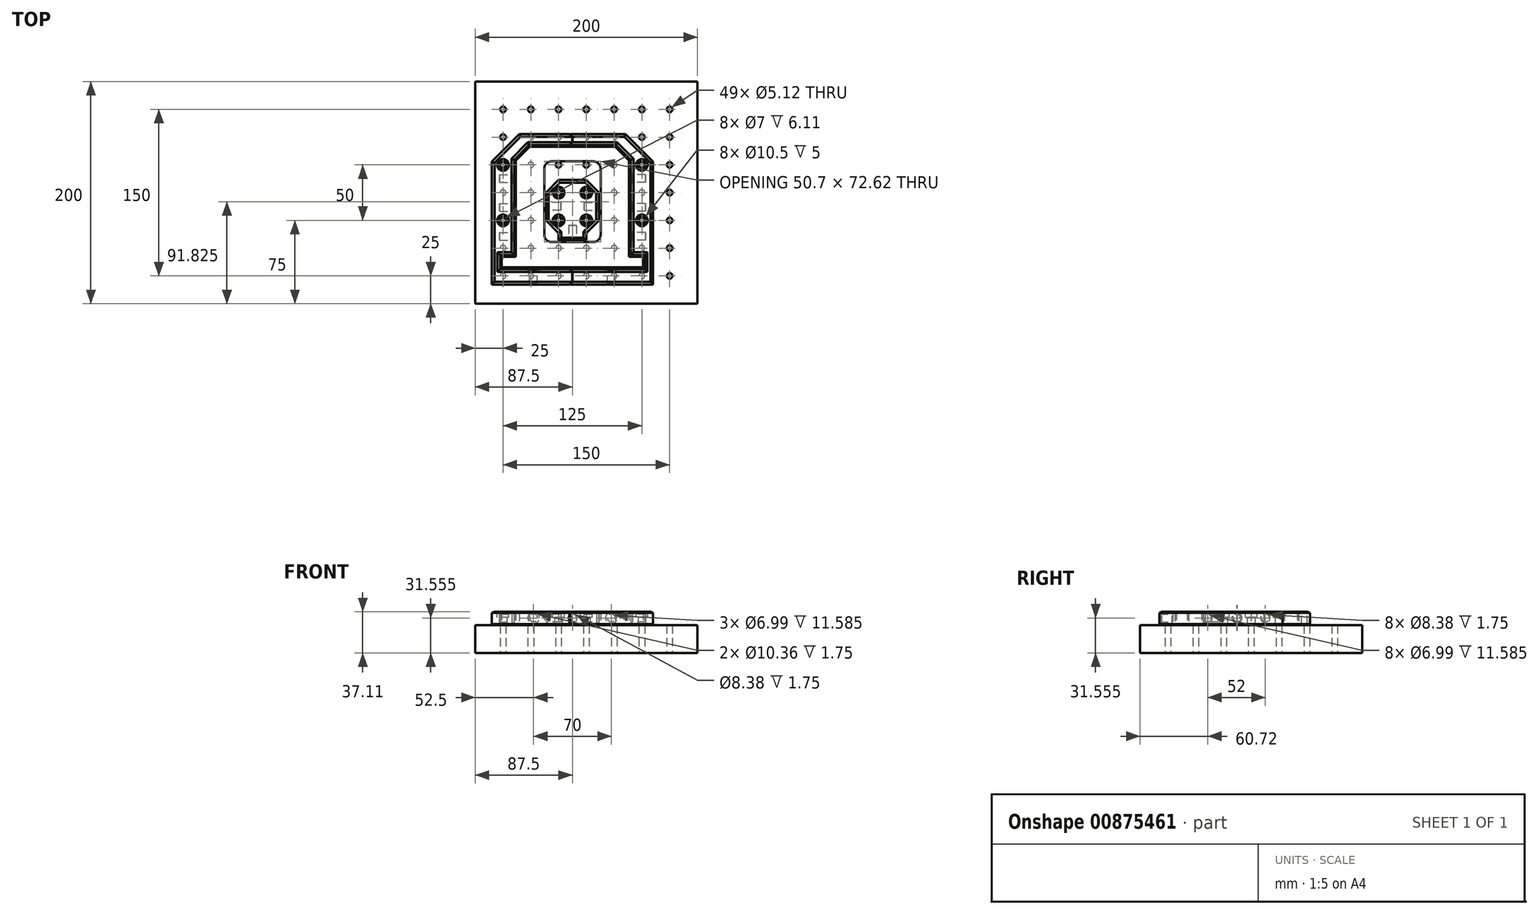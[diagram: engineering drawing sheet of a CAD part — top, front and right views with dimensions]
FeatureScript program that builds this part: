
annotation { "Feature Type Name" : "Feature", "Feature Type Description" : "" }
export const myFeature = defineFeature(function(context is Context, id is Id, definition is map)
    precondition{}
    {
        {
            assignVariable(context, id + "F0", {"name" : "plugdep1", "anyValue" : 13.33 * mm});
        }
        {
            assignVariable(context, id + "F1", {"name" : "plugdep2", "anyValue" : 1.75});
        }
        {
            var Q0;
            Q0=qCreatedBy(makeId("Top.planeOp"),FACE);
            var sketch = newSketch(context, id + "F2", { "sketchPlane" : qUnion([Q0])});
            skLineSegment(sketch, "E0.bottom", {"start": v(-100, 100) * mm, "end": v(100, 100) * mm});
            skLineSegment(sketch, "E0.top", {"start": v(-100, -100) * mm, "end": v(100, -100) * mm});
            skLineSegment(sketch, "E0.left", {"start": v(-100, 100) * mm, "end": v(-100, -100) * mm});
            skLineSegment(sketch, "E0.right", {"start": v(100, 100) * mm, "end": v(100, -100) * mm});
            skPoint(sketch, "E0.middle", {"position": v(0, 0) * mm});
            skCircle(sketch, "E1", {"center": v(-75, 75) * mm, "radius": 2.56 * mm});
            skCircle(sketch, "E2.0.1.0", {"center": v(-75, 50) * mm, "radius": 2.56 * mm});
            skCircle(sketch, "E2.0.2.0", {"center": v(-75, 25) * mm, "radius": 2.56 * mm});
            skCircle(sketch, "E2.0.3.0", {"center": v(-75, 0) * mm, "radius": 2.56 * mm});
            skCircle(sketch, "E2.0.4.0", {"center": v(-75, -25) * mm, "radius": 2.56 * mm});
            skCircle(sketch, "E2.0.5.0", {"center": v(-75, -50) * mm, "radius": 2.56 * mm});
            skCircle(sketch, "E2.0.6.0", {"center": v(-75, -75) * mm, "radius": 2.56 * mm});
            skCircle(sketch, "E2.1.0.0", {"center": v(-50, 75) * mm, "radius": 2.56 * mm});
            skCircle(sketch, "E2.1.1.0", {"center": v(-50, 50) * mm, "radius": 2.56 * mm});
            skCircle(sketch, "E2.1.2.0", {"center": v(-50, 25) * mm, "radius": 2.56 * mm});
            skCircle(sketch, "E2.1.3.0", {"center": v(-50, 0) * mm, "radius": 2.56 * mm});
            skCircle(sketch, "E2.1.4.0", {"center": v(-50, -25) * mm, "radius": 2.56 * mm});
            skCircle(sketch, "E2.1.5.0", {"center": v(-50, -50) * mm, "radius": 2.56 * mm});
            skCircle(sketch, "E2.1.6.0", {"center": v(-50, -75) * mm, "radius": 2.56 * mm});
            skCircle(sketch, "E2.2.0.0", {"center": v(-25, 75) * mm, "radius": 2.56 * mm});
            skCircle(sketch, "E2.2.1.0", {"center": v(-25, 50) * mm, "radius": 2.56 * mm});
            skCircle(sketch, "E2.2.2.0", {"center": v(-25, 25) * mm, "radius": 2.56 * mm});
            skCircle(sketch, "E2.2.3.0", {"center": v(-25, 0) * mm, "radius": 2.56 * mm});
            skCircle(sketch, "E2.2.4.0", {"center": v(-25, -25) * mm, "radius": 2.56 * mm});
            skCircle(sketch, "E2.2.5.0", {"center": v(-25, -50) * mm, "radius": 2.56 * mm});
            skCircle(sketch, "E2.2.6.0", {"center": v(-25, -75) * mm, "radius": 2.56 * mm});
            skCircle(sketch, "E2.3.0.0", {"center": v(0, 75) * mm, "radius": 2.56 * mm});
            skCircle(sketch, "E2.3.1.0", {"center": v(0, 50) * mm, "radius": 2.56 * mm});
            skCircle(sketch, "E2.3.2.0", {"center": v(0, 25) * mm, "radius": 2.56 * mm});
            skCircle(sketch, "E2.3.3.0", {"center": v(0, 0) * mm, "radius": 2.56 * mm});
            skCircle(sketch, "E2.3.4.0", {"center": v(0, -25) * mm, "radius": 2.56 * mm});
            skCircle(sketch, "E2.3.5.0", {"center": v(0, -50) * mm, "radius": 2.56 * mm});
            skCircle(sketch, "E2.3.6.0", {"center": v(0, -75) * mm, "radius": 2.56 * mm});
            skCircle(sketch, "E2.4.0.0", {"center": v(25, 75) * mm, "radius": 2.56 * mm});
            skCircle(sketch, "E2.4.1.0", {"center": v(25, 50) * mm, "radius": 2.56 * mm});
            skCircle(sketch, "E2.4.2.0", {"center": v(25, 25) * mm, "radius": 2.56 * mm});
            skCircle(sketch, "E2.4.3.0", {"center": v(25, 0) * mm, "radius": 2.56 * mm});
            skCircle(sketch, "E2.4.4.0", {"center": v(25, -25) * mm, "radius": 2.56 * mm});
            skCircle(sketch, "E2.4.5.0", {"center": v(25, -50) * mm, "radius": 2.56 * mm});
            skCircle(sketch, "E2.4.6.0", {"center": v(25, -75) * mm, "radius": 2.56 * mm});
            skCircle(sketch, "E2.5.0.0", {"center": v(50, 75) * mm, "radius": 2.56 * mm});
            skCircle(sketch, "E2.5.1.0", {"center": v(50, 50) * mm, "radius": 2.56 * mm});
            skCircle(sketch, "E2.5.2.0", {"center": v(50, 25) * mm, "radius": 2.56 * mm});
            skCircle(sketch, "E2.5.3.0", {"center": v(50, 0) * mm, "radius": 2.56 * mm});
            skCircle(sketch, "E2.5.4.0", {"center": v(50, -25) * mm, "radius": 2.56 * mm});
            skCircle(sketch, "E2.5.5.0", {"center": v(50, -50) * mm, "radius": 2.56 * mm});
            skCircle(sketch, "E2.5.6.0", {"center": v(50, -75) * mm, "radius": 2.56 * mm});
            skCircle(sketch, "E2.6.0.0", {"center": v(75, 75) * mm, "radius": 2.56 * mm});
            skCircle(sketch, "E2.6.1.0", {"center": v(75, 50) * mm, "radius": 2.56 * mm});
            skCircle(sketch, "E2.6.2.0", {"center": v(75, 25) * mm, "radius": 2.56 * mm});
            skCircle(sketch, "E2.6.3.0", {"center": v(75, 0) * mm, "radius": 2.56 * mm});
            skCircle(sketch, "E2.6.4.0", {"center": v(75, -25) * mm, "radius": 2.56 * mm});
            skCircle(sketch, "E2.6.5.0", {"center": v(75, -50) * mm, "radius": 2.56 * mm});
            skCircle(sketch, "E2.6.6.0", {"center": v(75, -75) * mm, "radius": 2.56 * mm});
            skLineSegment(sketch, "E2.direction1", {"start": v(-75, 75) * mm, "end": v(-50, 75) * mm, "construction": true});
            skLineSegment(sketch, "E2.direction2", {"start": v(-75, 75) * mm, "end": v(-75, 50) * mm, "construction": true});
            skSolve(sketch);
        }
        {
            var Q0;
            Q0 = qSketchRegion(id + "F2", true);
            extrude(context, id + "F3", {"entities" : qUnion([Q0]), "depth" : 25 * mm, "offsetDistance" : 25 * mm});
        }
        {
            var Q0;
            Q0=makeQuery(id+"F3.opExtrude","CAP_FACE",FACE,{"disambiguationData":[OSD([sQuery(id+"F2.wireOp",EDGE,"E0.bottom"),sQuery(id+"F2.wireOp",EDGE,"E0.top"),sQuery(id+"F2.wireOp",EDGE,"E0.left"),sQuery(id+"F2.wireOp",EDGE,"E0.right"),sQuery(id+"F2.wireOp",EDGE,"E1"),sQuery(id+"F2.wireOp",EDGE,"E2.0.1.0"),sQuery(id+"F2.wireOp",EDGE,"E2.0.2.0"),sQuery(id+"F2.wireOp",EDGE,"E2.0.3.0"),sQuery(id+"F2.wireOp",EDGE,"E2.0.4.0"),sQuery(id+"F2.wireOp",EDGE,"E2.0.5.0"),sQuery(id+"F2.wireOp",EDGE,"E2.0.6.0"),sQuery(id+"F2.wireOp",EDGE,"E2.1.0.0"),sQuery(id+"F2.wireOp",EDGE,"E2.1.1.0"),sQuery(id+"F2.wireOp",EDGE,"E2.1.2.0"),sQuery(id+"F2.wireOp",EDGE,"E2.1.3.0"),sQuery(id+"F2.wireOp",EDGE,"E2.1.4.0"),sQuery(id+"F2.wireOp",EDGE,"E2.1.5.0"),sQuery(id+"F2.wireOp",EDGE,"E2.1.6.0"),sQuery(id+"F2.wireOp",EDGE,"E2.2.0.0"),sQuery(id+"F2.wireOp",EDGE,"E2.2.1.0"),sQuery(id+"F2.wireOp",EDGE,"E2.2.2.0"),sQuery(id+"F2.wireOp",EDGE,"E2.2.3.0"),sQuery(id+"F2.wireOp",EDGE,"E2.2.4.0"),sQuery(id+"F2.wireOp",EDGE,"E2.2.5.0"),sQuery(id+"F2.wireOp",EDGE,"E2.2.6.0"),sQuery(id+"F2.wireOp",EDGE,"E2.3.0.0"),sQuery(id+"F2.wireOp",EDGE,"E2.3.1.0"),sQuery(id+"F2.wireOp",EDGE,"E2.3.2.0"),sQuery(id+"F2.wireOp",EDGE,"E2.3.3.0"),sQuery(id+"F2.wireOp",EDGE,"E2.3.4.0"),sQuery(id+"F2.wireOp",EDGE,"E2.3.5.0"),sQuery(id+"F2.wireOp",EDGE,"E2.3.6.0"),sQuery(id+"F2.wireOp",EDGE,"E2.4.0.0"),sQuery(id+"F2.wireOp",EDGE,"E2.4.1.0"),sQuery(id+"F2.wireOp",EDGE,"E2.4.2.0"),sQuery(id+"F2.wireOp",EDGE,"E2.4.3.0"),sQuery(id+"F2.wireOp",EDGE,"E2.4.4.0"),sQuery(id+"F2.wireOp",EDGE,"E2.4.5.0"),sQuery(id+"F2.wireOp",EDGE,"E2.4.6.0"),sQuery(id+"F2.wireOp",EDGE,"E2.5.0.0"),sQuery(id+"F2.wireOp",EDGE,"E2.5.1.0"),sQuery(id+"F2.wireOp",EDGE,"E2.5.2.0"),sQuery(id+"F2.wireOp",EDGE,"E2.5.3.0"),sQuery(id+"F2.wireOp",EDGE,"E2.5.4.0"),sQuery(id+"F2.wireOp",EDGE,"E2.5.5.0"),sQuery(id+"F2.wireOp",EDGE,"E2.5.6.0"),sQuery(id+"F2.wireOp",EDGE,"E2.6.0.0"),sQuery(id+"F2.wireOp",EDGE,"E2.6.1.0"),sQuery(id+"F2.wireOp",EDGE,"E2.6.2.0"),sQuery(id+"F2.wireOp",EDGE,"E2.6.3.0"),sQuery(id+"F2.wireOp",EDGE,"E2.6.4.0"),sQuery(id+"F2.wireOp",EDGE,"E2.6.5.0"),sQuery(id+"F2.wireOp",EDGE,"E2.6.6.0")])],"isStart":false});
            cPlane(context, id + "F4", {"entities" : qUnion([Q0]), "cplaneType" : CPlaneType.OFFSET, "offset" : 1 * mm, "width" : 150 * mm, "height" : 150 * mm});
        }
        {
            var Q0;
            Q0=qCreatedBy(id+"F4.planeOp",FACE);
            var sketch = newSketch(context, id + "F5", { "sketchPlane" : qUnion([Q0])});
            skLineSegment(sketch, "E3.bottom", {"start": v(-31.35, 28.14) * mm, "end": v(6.35, 28.14) * mm});
            skLineSegment(sketch, "E3.top", {"start": v(-31.35, -44.48) * mm, "end": v(6.35, -44.48) * mm});
            skLineSegment(sketch, "E3.left", {"start": v(-37.85, 21.64) * mm, "end": v(-37.85, -37.98) * mm});
            skLineSegment(sketch, "E3.right", {"start": v(12.85, 21.64) * mm, "end": v(12.85, -37.98) * mm});
            skPoint(sketch, "E3.middle", {"position": v(-12.5, -8.17) * mm});
            skLineSegment(sketch, "E4.bottom", {"start": v(-63.37, 41.33) * mm, "end": v(38.38, 41.33) * mm, "construction": true});
            skLineSegment(sketch, "E4.top", {"start": v(-63.37, -57.67) * mm, "end": v(38.38, -57.67) * mm});
            skLineSegment(sketch, "E4.left", {"start": v(-63.37, 41.33) * mm, "end": v(-63.37, -57.67) * mm, "construction": true});
            skLineSegment(sketch, "E4.right", {"start": v(38.38, 41.33) * mm, "end": v(38.38, -57.67) * mm, "construction": true});
            skLineSegment(sketch, "E5.bottom", {"start": v(-76.06, -57.67) * mm, "end": v(51.06, -57.67) * mm});
            skLineSegment(sketch, "E5.top", {"start": v(-76.06, -67.32) * mm, "end": v(51.06, -67.32) * mm});
            skLineSegment(sketch, "E5.left", {"start": v(-76.06, -57.67) * mm, "end": v(-76.06, -67.32) * mm});
            skLineSegment(sketch, "E5.right", {"start": v(51.06, -57.67) * mm, "end": v(51.06, -67.32) * mm});
            skPoint(sketch, "E5.middle", {"position": v(-12.5, -62.5) * mm});
            skLineSegment(sketch, "E6", {"start": v(-51.04, 41.33) * mm, "end": v(-63.37, 29) * mm});
            skLineSegment(sketch, "E7", {"start": v(26.04, 41.33) * mm, "end": v(38.38, 29) * mm});
            skPoint(sketch, "E8.visualSharp", {"position": v(-37.85, 28.14) * mm});
            skArc(sketch, "E8.filletArc", {"start": v(-31.35, 28.14) * mm, "mid": v(-35.95, 26.23) * mm, "end": v(-37.85, 21.64) * mm});
            skPoint(sketch, "E9.visualSharp", {"position": v(12.85, 28.14) * mm});
            skArc(sketch, "E9.filletArc", {"start": v(12.85, 21.64) * mm, "mid": v(10.95, 26.23) * mm, "end": v(6.35, 28.14) * mm});
            skPoint(sketch, "E10.visualSharp", {"position": v(12.85, -44.48) * mm});
            skArc(sketch, "E10.filletArc", {"start": v(6.35, -44.48) * mm, "mid": v(10.95, -42.58) * mm, "end": v(12.85, -37.98) * mm});
            skPoint(sketch, "E11.visualSharp", {"position": v(-37.85, -44.48) * mm});
            skArc(sketch, "E11.filletArc", {"start": v(-37.85, -37.98) * mm, "mid": v(-35.95, -42.58) * mm, "end": v(-31.35, -44.48) * mm});
            skLineSegment(sketch, "E12", {"start": v(-63.37, -57.67) * mm, "end": v(-63.37, 29) * mm});
            skLineSegment(sketch, "E13", {"start": v(-51.04, 41.33) * mm, "end": v(26.04, 41.33) * mm});
            skLineSegment(sketch, "E14", {"start": v(38.38, 29) * mm, "end": v(38.38, -57.67) * mm});
            skLineSegment(sketch, "E15", {"start": v(-63.37, 41.33) * mm, "end": v(-57.2, 35.16) * mm, "construction": true});
            skLineSegment(sketch, "E16", {"start": v(38.38, 41.33) * mm, "end": v(32.2, 35.16) * mm, "construction": true});
            skLineSegment(sketch, "E17", {"start": v(-25, 50) * mm, "end": v(0, 50) * mm, "construction": true});
            skPoint(sketch, "E18", {"position": v(-12.5, 50) * mm});
            skLineSegment(sketch, "E19", {"start": v(-37.85, -8.17) * mm, "end": v(-63.37, -8.17) * mm, "construction": true});
            skLineSegment(sketch, "E20", {"start": v(12.85, -8.17) * mm, "end": v(38.38, -8.17) * mm, "construction": true});
            skLineSegment(sketch, "E21", {"start": v(75, -75) * mm, "end": v(75, -50) * mm, "construction": true});
            skPoint(sketch, "E22", {"position": v(75, -62.5) * mm});
            skPoint(sketch, "E23", {"position": v(51.06, -62.5) * mm});
            skSolve(sketch);
        }
        {
            var Q0;
            Q0 = qSketchRegion(id + "F5", true);
            extrude(context, id + "F6", {"entities" : qUnion([Q0]), "depth" : 11.1 * mm, "offsetDistance" : 25 * mm});
        }
        {
            var Q0;
            Q0=qCreatedBy(id+"F4.planeOp",FACE);
            var sketch = newSketch(context, id + "F7", { "sketchPlane" : qUnion([Q0])});
            skLineSegment(sketch, "E24", {"start": v(-64.87, -56.17) * mm, "end": v(-77.56, -56.17) * mm});
            skLineSegment(sketch, "E25", {"start": v(-77.56, -56.17) * mm, "end": v(-77.56, -68.82) * mm});
            skLineSegment(sketch, "E26", {"start": v(-77.56, -68.82) * mm, "end": v(52.56, -68.82) * mm});
            skLineSegment(sketch, "E27", {"start": v(52.56, -68.82) * mm, "end": v(52.56, -56.17) * mm});
            skLineSegment(sketch, "E28", {"start": v(52.56, -56.17) * mm, "end": v(39.88, -56.17) * mm});
            skLineSegment(sketch, "E29", {"start": v(39.87, -56.17) * mm, "end": v(39.88, 29.61) * mm});
            skLineSegment(sketch, "E30", {"start": v(39.88, 29.61) * mm, "end": v(26.66, 42.83) * mm});
            skLineSegment(sketch, "E31", {"start": v(26.66, 42.83) * mm, "end": v(-51.66, 42.83) * mm});
            skLineSegment(sketch, "E32", {"start": v(-51.66, 42.83) * mm, "end": v(-64.87, 29.61) * mm});
            skLineSegment(sketch, "E33", {"start": v(-64.87, 29.61) * mm, "end": v(-64.88, -56.17) * mm});
            skLineSegment(sketch, "E34", {"start": v(-64.87, -13.28) * mm, "end": v(-63.37, -13.28) * mm, "construction": true});
            skLineSegment(sketch, "E35", {"start": v(39.88, -13.28) * mm, "end": v(38.38, -13.28) * mm, "construction": true});
            skLineSegment(sketch, "E36", {"start": v(-12.5, -68.82) * mm, "end": v(-12.5, -67.32) * mm, "construction": true});
            skLineSegment(sketch, "E37", {"start": v(-77.56, -62.5) * mm, "end": v(-76.06, -62.5) * mm, "construction": true});
            skLineSegment(sketch, "E38", {"start": v(52.56, -62.5) * mm, "end": v(51.06, -62.5) * mm, "construction": true});
            skLineSegment(sketch, "E39", {"start": v(-12.5, 42.83) * mm, "end": v(-12.5, 41.33) * mm, "construction": true});
            skLineSegment(sketch, "E40", {"start": v(-58.27, 36.22) * mm, "end": v(-57.2, 35.16) * mm, "construction": true});
            skLineSegment(sketch, "E41", {"start": v(33.27, 36.22) * mm, "end": v(32.2, 35.16) * mm, "construction": true});
            skLineSegment(sketch, "E42", {"start": v(-71.22, -56.17) * mm, "end": v(-71.22, -57.67) * mm, "construction": true});
            skLineSegment(sketch, "E43", {"start": v(46.22, -56.17) * mm, "end": v(46.22, -57.67) * mm, "construction": true});
            skLineSegment(sketch, "E44", {"start": v(-85.12, -82.82) * mm, "end": v(60.13, -82.82) * mm});
            skLineSegment(sketch, "E45", {"start": v(60.12, -82.82) * mm, "end": v(60.12, 28) * mm});
            skLineSegment(sketch, "E46", {"start": v(60.13, 28) * mm, "end": v(35.3, 52.83) * mm});
            skLineSegment(sketch, "E47", {"start": v(35.3, 52.83) * mm, "end": v(-60.3, 52.83) * mm});
            skLineSegment(sketch, "E48", {"start": v(-60.3, 52.83) * mm, "end": v(-85.12, 28) * mm});
            skLineSegment(sketch, "E49", {"start": v(-85.12, 28) * mm, "end": v(-85.13, -82.82) * mm});
            skLineSegment(sketch, "E50", {"start": v(-85.12, -27.4) * mm, "end": v(-64.87, -27.4) * mm, "construction": true});
            skLineSegment(sketch, "E51", {"start": v(60.13, -27.4) * mm, "end": v(39.88, -27.4) * mm, "construction": true});
            skLineSegment(sketch, "E52", {"start": v(-12.5, -82.82) * mm, "end": v(-12.5, -68.82) * mm, "construction": true});
            skLineSegment(sketch, "E53", {"start": v(-12.5, 52.83) * mm, "end": v(-12.5, 42.83) * mm, "construction": true});
            skPoint(sketch, "E54", {"position": v(-75, -27.4) * mm});
            skPoint(sketch, "E55", {"position": v(-75, 0) * mm});
            skPoint(sketch, "E56", {"position": v(50, 0) * mm});
            skPoint(sketch, "E57", {"position": v(50, -27.4) * mm});
            skLineSegment(sketch, "E58", {"start": v(-72.72, 40.42) * mm, "end": v(-63.4, 31.1) * mm, "construction": true});
            skLineSegment(sketch, "E59", {"start": v(47.72, 40.42) * mm, "end": v(38.4, 31.1) * mm, "construction": true});
            skPoint(sketch, "E60", {"position": v(-12.5, 47.83) * mm});
            skPoint(sketch, "E61", {"position": v(-12.5, -75.82) * mm});
            skCircle(sketch, "E62", {"center": v(-75, 25) * mm, "radius": 3.5 * mm});
            skCircle(sketch, "E63", {"center": v(-75, -25) * mm, "radius": 3.5 * mm});
            skCircle(sketch, "E64", {"center": v(50, 25) * mm, "radius": 3.5 * mm});
            skCircle(sketch, "E65", {"center": v(50, -25) * mm, "radius": 3.5 * mm});
            skLineSegment(sketch, "E66", {"start": v(-36.35, -25) * mm, "end": v(-25, -36.35) * mm});
            skLineSegment(sketch, "E67", {"start": v(-25, -36.35) * mm, "end": v(0, -36.35) * mm});
            skLineSegment(sketch, "E68", {"start": v(0, -36.35) * mm, "end": v(11.35, -25) * mm});
            skLineSegment(sketch, "E69", {"start": v(11.35, -25) * mm, "end": v(11.35, 0) * mm});
            skLineSegment(sketch, "E70", {"start": v(11.35, 0) * mm, "end": v(0, 11.35) * mm});
            skLineSegment(sketch, "E71", {"start": v(0, 11.35) * mm, "end": v(-25, 11.35) * mm});
            skLineSegment(sketch, "E72", {"start": v(-25, 11.35) * mm, "end": v(-36.35, 0) * mm});
            skLineSegment(sketch, "E73", {"start": v(-36.35, 0) * mm, "end": v(-36.35, -25) * mm});
            skLineSegment(sketch, "E74.bottom", {"start": v(-22.53, -2.47) * mm, "end": v(-2.47, -2.47) * mm, "construction": true});
            skLineSegment(sketch, "E74.top", {"start": v(-22.53, -22.53) * mm, "end": v(-2.47, -22.53) * mm, "construction": true});
            skLineSegment(sketch, "E74.left", {"start": v(-22.53, -2.47) * mm, "end": v(-22.53, -22.53) * mm, "construction": true});
            skLineSegment(sketch, "E74.right", {"start": v(-2.47, -2.47) * mm, "end": v(-2.47, -22.53) * mm, "construction": true});
            skPoint(sketch, "E74.middle", {"position": v(-12.5, -12.5) * mm});
            skLineSegment(sketch, "E75", {"start": v(-30.67, 5.68) * mm, "end": v(-22.53, -2.47) * mm, "construction": true});
            skLineSegment(sketch, "E76", {"start": v(-2.47, -2.47) * mm, "end": v(5.68, 5.68) * mm, "construction": true});
            skPoint(sketch, "E76.endSnap0", {"position": v(5.68, 5.68) * mm});
            skLineSegment(sketch, "E77", {"start": v(5.67, -30.68) * mm, "end": v(-2.47, -22.53) * mm, "construction": true});
            skLineSegment(sketch, "E78", {"start": v(-30.67, -30.67) * mm, "end": v(-22.53, -22.53) * mm, "construction": true});
            skLineSegment(sketch, "E79", {"start": v(-36.35, -12.5) * mm, "end": v(-37.85, -12.5) * mm, "construction": true});
            skLineSegment(sketch, "E80", {"start": v(11.35, -12.5) * mm, "end": v(12.85, -12.5) * mm, "construction": true});
            skPoint(sketch, "E81", {"position": v(-25, -25) * mm});
            skPoint(sketch, "E82", {"position": v(-25, 0) * mm});
            skPoint(sketch, "E83", {"position": v(0, -25) * mm});
            skCircle(sketch, "E84", {"center": v(-25, 0) * mm, "radius": 3.5 * mm});
            skCircle(sketch, "E85", {"center": v(-25, -25) * mm, "radius": 3.5 * mm});
            skCircle(sketch, "E86", {"center": v(0, -25) * mm, "radius": 3.5 * mm});
            skCircle(sketch, "E87", {"center": v(0, 0) * mm, "radius": 3.5 * mm});
            skLineSegment(sketch, "E88", {"start": v(-25, -36.35) * mm, "end": v(-25, -42.98) * mm});
            skLineSegment(sketch, "E89", {"start": v(-25, -42.98) * mm, "end": v(0, -42.98) * mm});
            skLineSegment(sketch, "E90", {"start": v(0, -42.98) * mm, "end": v(0, -36.35) * mm});
            skLineSegment(sketch, "E91", {"start": v(-12.5, -42.98) * mm, "end": v(-12.5, -44.48) * mm, "construction": true});
            skPoint(sketch, "E92", {"position": v(-75, 38.13) * mm});
            skSolve(sketch);
        }
        {
            var Q0;
            Q0 = qSketchRegion(id + "F7", true);
            var Q1;
            Q1=makeQuery(id+"F7.imprint","IMPRINT",FACE,{"disambiguationData":[TD([[makeQuery(id+"F7.imprint","IMPRINT",EDGE,{"derivedFrom":sQuery(id+"F7.wireOp",EDGE,"E66")}),1.0]])]});
            var Q2;
            Q2=makeQuery(id+"F7.imprint","IMPRINT",FACE,{"disambiguationData":[TD([[makeQuery(id+"F7.imprint","IMPRINT",EDGE,{"derivedFrom":sQuery(id+"F7.wireOp",EDGE,"E67")}),-1.0]])]});
            var Q3;
            Q3=makeQuery(id+"F6.opExtrude","CAP_FACE",FACE,{"disambiguationData":[OSD([sQuery(id+"F5.wireOp",EDGE,"E3.bottom"),sQuery(id+"F5.wireOp",EDGE,"E3.top"),sQuery(id+"F5.wireOp",EDGE,"E3.left"),sQuery(id+"F5.wireOp",EDGE,"E3.right"),sQuery(id+"F5.wireOp",EDGE,"E5.bottom"),sQuery(id+"F5.wireOp",EDGE,"E5.top"),sQuery(id+"F5.wireOp",EDGE,"E5.left"),sQuery(id+"F5.wireOp",EDGE,"E5.right"),sQuery(id+"F5.wireOp",EDGE,"E6"),sQuery(id+"F5.wireOp",EDGE,"E7"),sQuery(id+"F5.wireOp",EDGE,"E8.filletArc"),sQuery(id+"F5.wireOp",EDGE,"E9.filletArc"),sQuery(id+"F5.wireOp",EDGE,"E10.filletArc"),sQuery(id+"F5.wireOp",EDGE,"E11.filletArc"),sQuery(id+"F5.wireOp",EDGE,"E12"),sQuery(id+"F5.wireOp",EDGE,"E13"),sQuery(id+"F5.wireOp",EDGE,"E14")])],"isStart":false});
            extrude(context, id + "F8", {"entities" : qUnion([Q0, Q1, Q2]), "endBound" : BoundingType.UP_TO_SURFACE, "depth" : 25 * mm, "endBoundEntityFace" : qUnion([Q3]), "offsetDistance" : 25 * mm});
        }
        {
            var Q0;
            Q0=makeQuery(id+"F8.opExtrude","CAP_FACE",FACE,{"disambiguationData":[OSD([sQuery(id+"F7.wireOp",EDGE,"E24"),sQuery(id+"F7.wireOp",EDGE,"E25"),sQuery(id+"F7.wireOp",EDGE,"E26"),sQuery(id+"F7.wireOp",EDGE,"E27"),sQuery(id+"F7.wireOp",EDGE,"E28"),sQuery(id+"F7.wireOp",EDGE,"E29"),sQuery(id+"F7.wireOp",EDGE,"E30"),sQuery(id+"F7.wireOp",EDGE,"E31"),sQuery(id+"F7.wireOp",EDGE,"E32"),sQuery(id+"F7.wireOp",EDGE,"E33"),sQuery(id+"F7.wireOp",EDGE,"E44"),sQuery(id+"F7.wireOp",EDGE,"E45"),sQuery(id+"F7.wireOp",EDGE,"E46"),sQuery(id+"F7.wireOp",EDGE,"E47"),sQuery(id+"F7.wireOp",EDGE,"E48"),sQuery(id+"F7.wireOp",EDGE,"E49"),sQuery(id+"F7.wireOp",EDGE,"E62"),sQuery(id+"F7.wireOp",EDGE,"E63"),sQuery(id+"F7.wireOp",EDGE,"E64"),sQuery(id+"F7.wireOp",EDGE,"E65")])],"isStart":false});
            var sketch = newSketch(context, id + "F9", { "sketchPlane" : qUnion([Q0])});
            skCircle(sketch, "E93", {"center": v(-75, 25) * mm, "radius": 5.25 * mm});
            skCircle(sketch, "E94", {"center": v(-75, -25) * mm, "radius": 5.25 * mm});
            skCircle(sketch, "E95", {"center": v(50, 25) * mm, "radius": 5.25 * mm});
            skCircle(sketch, "E96", {"center": v(50, -25) * mm, "radius": 5.25 * mm});
            skCircle(sketch, "E97", {"center": v(0, 0) * mm, "radius": 5.25 * mm});
            skCircle(sketch, "E98", {"center": v(0, -25) * mm, "radius": 5.25 * mm});
            skCircle(sketch, "E99", {"center": v(-25, -25) * mm, "radius": 5.25 * mm});
            skCircle(sketch, "E100", {"center": v(-25, 0) * mm, "radius": 5.25 * mm});
            skSolve(sketch);
        }
        {
            var Q0;
            Q0 = qSketchRegion(id + "F9", true);
            extrude(context, id + "F10", {"entities" : qUnion([Q0]), "operationType" : NewBodyOperationType.REMOVE, "oppositeDirection" : true, "depth" : 5 * mm, "offsetDistance" : 25 * mm});
        }
        {
            var Q0;
            Q0=makeQuery(id+"F8.opExtrude","CAP_EDGE",EDGE,{"disambiguationData":[OSD([sQuery(id+"F7.wireOp",EDGE,"E71")])],"isStart":false});
            var Q1;
            Q1=makeQuery(id+"F8.opExtrude","CAP_EDGE",EDGE,{"disambiguationData":[OSD([sQuery(id+"F7.wireOp",EDGE,"E72")])],"isStart":false});
            var Q2;
            Q2=makeQuery(id+"F8.opExtrude","CAP_EDGE",EDGE,{"disambiguationData":[OSD([sQuery(id+"F7.wireOp",EDGE,"E73")])],"isStart":false});
            var Q3;
            Q3=makeQuery(id+"F8.opExtrude","CAP_EDGE",EDGE,{"disambiguationData":[OSD([sQuery(id+"F7.wireOp",EDGE,"E66")])],"isStart":false});
            var Q4;
            Q4=makeQuery(id+"F8.opExtrude","CAP_EDGE",EDGE,{"disambiguationData":[OSD([sQuery(id+"F7.wireOp",EDGE,"E88")])],"isStart":false});
            var Q5;
            Q5=makeQuery(id+"F8.opExtrude","CAP_EDGE",EDGE,{"disambiguationData":[OSD([sQuery(id+"F7.wireOp",EDGE,"E89")])],"isStart":false});
            var Q6;
            Q6=makeQuery(id+"F8.opExtrude","CAP_EDGE",EDGE,{"disambiguationData":[OSD([sQuery(id+"F7.wireOp",EDGE,"E90")])],"isStart":false});
            var Q7;
            Q7=makeQuery(id+"F8.opExtrude","CAP_EDGE",EDGE,{"disambiguationData":[OSD([sQuery(id+"F7.wireOp",EDGE,"E68")])],"isStart":false});
            var Q8;
            Q8=makeQuery(id+"F8.opExtrude","CAP_EDGE",EDGE,{"disambiguationData":[OSD([sQuery(id+"F7.wireOp",EDGE,"E69")])],"isStart":false});
            var Q9;
            Q9=makeQuery(id+"F8.opExtrude","CAP_EDGE",EDGE,{"disambiguationData":[OSD([sQuery(id+"F7.wireOp",EDGE,"E70")])],"isStart":false});
            chamfer(context, id + "F11", {"entities" : qUnion([Q0, Q1, Q2, Q3, Q4, Q5, Q6, Q7, Q8, Q9]), "chamferType" : ChamferType.TWO_OFFSETS, "width1" : 2.5 * mm, "oppositeDirection" : false, "width2" : 1 * mm});
        }
        {
            var Q0;
            Q0=makeQuery(id+"F8.opExtrude","CAP_EDGE",EDGE,{"disambiguationData":[OSD([sQuery(id+"F7.wireOp",EDGE,"E33")])],"isStart":false});
            var Q1;
            Q1=makeQuery(id+"F8.opExtrude","CAP_EDGE",EDGE,{"disambiguationData":[OSD([sQuery(id+"F7.wireOp",EDGE,"E32")])],"isStart":false});
            var Q2;
            Q2=makeQuery(id+"F8.opExtrude","CAP_EDGE",EDGE,{"disambiguationData":[OSD([sQuery(id+"F7.wireOp",EDGE,"E31")])],"isStart":false});
            var Q3;
            Q3=makeQuery(id+"F8.opExtrude","CAP_EDGE",EDGE,{"disambiguationData":[OSD([sQuery(id+"F7.wireOp",EDGE,"E30")])],"isStart":false});
            var Q4;
            Q4=makeQuery(id+"F8.opExtrude","CAP_EDGE",EDGE,{"disambiguationData":[OSD([sQuery(id+"F7.wireOp",EDGE,"E29")])],"isStart":false});
            var Q5;
            Q5=makeQuery(id+"F8.opExtrude","CAP_EDGE",EDGE,{"disambiguationData":[OSD([sQuery(id+"F7.wireOp",EDGE,"E28")])],"isStart":false});
            var Q6;
            Q6=makeQuery(id+"F8.opExtrude","CAP_EDGE",EDGE,{"disambiguationData":[OSD([sQuery(id+"F7.wireOp",EDGE,"E27")])],"isStart":false});
            var Q7;
            Q7=makeQuery(id+"F8.opExtrude","CAP_EDGE",EDGE,{"disambiguationData":[OSD([sQuery(id+"F7.wireOp",EDGE,"E26")])],"isStart":false});
            var Q8;
            Q8=makeQuery(id+"F8.opExtrude","CAP_EDGE",EDGE,{"disambiguationData":[OSD([sQuery(id+"F7.wireOp",EDGE,"E25")])],"isStart":false});
            var Q9;
            Q9=makeQuery(id+"F8.opExtrude","CAP_EDGE",EDGE,{"disambiguationData":[OSD([sQuery(id+"F7.wireOp",EDGE,"E24")])],"isStart":false});
            var Q10;
            Q10=makeQuery(id+"F8.opExtrude","CAP_EDGE",EDGE,{"disambiguationData":[OSD([sQuery(id+"F7.wireOp",EDGE,"E44")])],"isStart":false});
            var Q11;
            Q11=makeQuery(id+"F8.opExtrude","CAP_EDGE",EDGE,{"disambiguationData":[OSD([sQuery(id+"F7.wireOp",EDGE,"E49")])],"isStart":false});
            var Q12;
            Q12=makeQuery(id+"F8.opExtrude","CAP_EDGE",EDGE,{"disambiguationData":[OSD([sQuery(id+"F7.wireOp",EDGE,"E48")])],"isStart":false});
            var Q13;
            Q13=makeQuery(id+"F8.opExtrude","CAP_EDGE",EDGE,{"disambiguationData":[OSD([sQuery(id+"F7.wireOp",EDGE,"E47")])],"isStart":false});
            var Q14;
            Q14=makeQuery(id+"F8.opExtrude","CAP_EDGE",EDGE,{"disambiguationData":[OSD([sQuery(id+"F7.wireOp",EDGE,"E46")])],"isStart":false});
            var Q15;
            Q15=makeQuery(id+"F8.opExtrude","CAP_EDGE",EDGE,{"disambiguationData":[OSD([sQuery(id+"F7.wireOp",EDGE,"E45")])],"isStart":false});
            chamfer(context, id + "F12", {"entities" : qUnion([Q0, Q1, Q2, Q3, Q4, Q5, Q6, Q7, Q8, Q9, Q10, Q11, Q12, Q13, Q14, Q15]), "chamferType" : ChamferType.TWO_OFFSETS, "width1" : 1 * mm, "oppositeDirection" : false, "width2" : 2.5 * mm, "tangentPropagation" : true});
        }
        {
            var Q0;
            Q0=makeQuery(id+"F8.opExtrude","SWEPT_FACE",FACE,{"disambiguationData":[OSD([sQuery(id+"F7.wireOp",EDGE,"E69")])]});
            var sketch = newSketch(context, id + "F13", { "sketchPlane" : qUnion([Q0])});
            skCircle(sketch, "E101", {"center": v(-12.5, 31.55) * mm, "radius": 3.5 * mm});
            skLineSegment(sketch, "E102", {"start": v(-25, 31.55) * mm, "end": v(0, 31.55) * mm, "construction": true});
            skLineSegment(sketch, "E103", {"start": v(-12.5, 26) * mm, "end": v(-12.5, 37.11) * mm, "construction": true});
            skSolve(sketch);
        }
        {
            var Q0;
            Q0 = qSketchRegion(id + "F13", true);
            extrude(context, id + "F14", {"entities" : qUnion([Q0]), "operationType" : NewBodyOperationType.REMOVE, "oppositeDirection" : true, "depth" : getVariable(context, 'plugdep1'), "offsetDistance" : 25 * mm});
        }
        {
            var Q0;
            Q0=makeQuery(id+"F8.opExtrude","SWEPT_FACE",FACE,{"disambiguationData":[OSD([sQuery(id+"F7.wireOp",EDGE,"E69")])]});
            var sketch = newSketch(context, id + "F15", { "sketchPlane" : qUnion([Q0])});
            skLineSegment(sketch, "E104", {"start": v(-25, 31.55) * mm, "end": v(0, 31.55) * mm, "construction": true});
            skLineSegment(sketch, "E105", {"start": v(-12.5, 26) * mm, "end": v(-12.5, 37.11) * mm, "construction": true});
            skCircle(sketch, "E106", {"center": v(-12.5, 31.55) * mm, "radius": 4.2 * mm});
            skSolve(sketch);
        }
        {
            var Q0;
            Q0 = qSketchRegion(id + "F15", true);
            extrude(context, id + "F16", {"entities" : qUnion([Q0]), "operationType" : NewBodyOperationType.REMOVE, "oppositeDirection" : true, "depth" : (getVariable(context, 'plugdep2')) * mm, "offsetDistance" : 25 * mm});
        }
        {
            var Q0;
            Q0=makeQuery(id+"F8.opExtrude","SWEPT_FACE",FACE,{"disambiguationData":[OSD([sQuery(id+"F7.wireOp",EDGE,"E73")])]});
            var sketch = newSketch(context, id + "F17", { "sketchPlane" : qUnion([Q0])});
            skLineSegment(sketch, "E107", {"start": v(12.5, 37.11) * mm, "end": v(12.5, 26) * mm, "construction": true});
            skPoint(sketch, "E107.startSnap0", {"position": v(12.5, 36.11) * mm});
            skCircle(sketch, "E108", {"center": v(12.5, 31.55) * mm, "radius": 3.5 * mm});
            skSolve(sketch);
        }
        {
            var Q0;
            Q0 = qSketchRegion(id + "F17", true);
            extrude(context, id + "F18", {"entities" : qUnion([Q0]), "operationType" : NewBodyOperationType.REMOVE, "oppositeDirection" : true, "depth" : getVariable(context, 'plugdep1'), "offsetDistance" : 25 * mm});
        }
        {
            var Q0;
            Q0=makeQuery(id+"F8.opExtrude","SWEPT_FACE",FACE,{"disambiguationData":[OSD([sQuery(id+"F7.wireOp",EDGE,"E73")])]});
            var sketch = newSketch(context, id + "F19", { "sketchPlane" : qUnion([Q0])});
            skLineSegment(sketch, "E109", {"start": v(12.5, 26) * mm, "end": v(12.5, 37.11) * mm, "construction": true});
            skCircle(sketch, "E110", {"center": v(12.5, 31.55) * mm, "radius": 4.2 * mm});
            skSolve(sketch);
        }
        {
            var Q0;
            Q0 = qSketchRegion(id + "F19", true);
            extrude(context, id + "F20", {"entities" : qUnion([Q0]), "operationType" : NewBodyOperationType.REMOVE, "oppositeDirection" : true, "depth" : (getVariable(context, 'plugdep2')) * mm, "offsetDistance" : 25 * mm});
        }
        {
            var Q0;
            Q0=makeQuery(id+"F8.opExtrude","SWEPT_FACE",FACE,{"disambiguationData":[OSD([sQuery(id+"F7.wireOp",EDGE,"E89")])]});
            var sketch = newSketch(context, id + "F21", { "sketchPlane" : qUnion([Q0])});
            skLineSegment(sketch, "E111", {"start": v(-12.5, 26) * mm, "end": v(-12.5, 37.11) * mm, "construction": true});
            skCircle(sketch, "E112", {"center": v(-12.5, 31.55) * mm, "radius": 3.5 * mm});
            skSolve(sketch);
        }
        {
            var Q0;
            Q0 = qSketchRegion(id + "F21", true);
            extrude(context, id + "F22", {"entities" : qUnion([Q0]), "operationType" : NewBodyOperationType.REMOVE, "oppositeDirection" : true, "depth" : getVariable(context, 'plugdep1'), "offsetDistance" : 25 * mm});
        }
        {
            var Q0;
            Q0=makeQuery(id+"F8.opExtrude","SWEPT_FACE",FACE,{"disambiguationData":[OSD([sQuery(id+"F7.wireOp",EDGE,"E89")])]});
            var sketch = newSketch(context, id + "F23", { "sketchPlane" : qUnion([Q0])});
            skLineSegment(sketch, "E113", {"start": v(-12.5, 26) * mm, "end": v(-12.5, 37.11) * mm, "construction": true});
            skCircle(sketch, "E114", {"center": v(-12.5, 31.55) * mm, "radius": 4.2 * mm});
            skSolve(sketch);
        }
        {
            var Q0;
            Q0 = qSketchRegion(id + "F23", true);
            extrude(context, id + "F24", {"entities" : qUnion([Q0]), "operationType" : NewBodyOperationType.REMOVE, "oppositeDirection" : true, "depth" : (getVariable(context, 'plugdep2')) * mm, "offsetDistance" : 25 * mm});
        }
        {
            var Q0;
            Q0=makeQuery(id+"F8.opExtrude","SWEPT_FACE",FACE,{"disambiguationData":[OSD([sQuery(id+"F7.wireOp",EDGE,"E33")])]});
            var sketch = newSketch(context, id + "F25", { "sketchPlane" : qUnion([Q0])});
            skLineSegment(sketch, "E115", {"start": v(-39.28, 26) * mm, "end": v(-39.28, 37.11) * mm, "construction": true});
            skLineSegment(sketch, "E116", {"start": v(-13.28, 26) * mm, "end": v(-13.28, 37.11) * mm, "construction": true});
            skLineSegment(sketch, "E117", {"start": v(12.72, 26) * mm, "end": v(12.72, 37.11) * mm, "construction": true});
            skLineSegment(sketch, "E118", {"start": v(-39.28, 31.55) * mm, "end": v(-13.28, 31.55) * mm, "construction": true});
            skLineSegment(sketch, "E119", {"start": v(-13.28, 31.55) * mm, "end": v(12.72, 31.55) * mm, "construction": true});
            skCircle(sketch, "E120", {"center": v(-39.28, 31.55) * mm, "radius": 3.5 * mm});
            skCircle(sketch, "E121", {"center": v(-13.28, 31.55) * mm, "radius": 3.5 * mm});
            skCircle(sketch, "E122", {"center": v(12.72, 31.55) * mm, "radius": 3.5 * mm});
            skLineSegment(sketch, "E123", {"start": v(-39.28, 31.55) * mm, "end": v(-56.18, 31.55) * mm, "construction": true});
            skPoint(sketch, "E123.endSnap0", {"position": v(-56.18, 31.06) * mm});
            skLineSegment(sketch, "E124", {"start": v(12.72, 31.55) * mm, "end": v(29.61, 31.55) * mm, "construction": true});
            skSolve(sketch);
        }
        {
            var Q0;
            Q0 = qSketchRegion(id + "F25", true);
            extrude(context, id + "F26", {"entities" : qUnion([Q0]), "operationType" : NewBodyOperationType.REMOVE, "oppositeDirection" : true, "depth" : getVariable(context, 'plugdep1'), "offsetDistance" : 25 * mm});
        }
        {
            var Q0;
            Q0=makeQuery(id+"F25.imprint","IMPRINT",FACE,{"disambiguationData":[TD([[makeQuery(id+"F25.imprint","IMPRINT",EDGE,{"derivedFrom":sQuery(id+"F25.wireOp",EDGE,"E120")}),-1.0]])]});
            var sketch = newSketch(context, id + "F27", { "sketchPlane" : qUnion([Q0])});
            skCircle(sketch, "E125", {"center": v(-39.28, 31.55) * mm, "radius": 4.2 * mm});
            skCircle(sketch, "E126", {"center": v(-13.28, 31.55) * mm, "radius": 4.2 * mm});
            skCircle(sketch, "E127", {"center": v(12.72, 31.55) * mm, "radius": 4.2 * mm});
            skSolve(sketch);
        }
        {
            var Q0;
            Q0 = qSketchRegion(id + "F27", true);
            extrude(context, id + "F28", {"entities" : qUnion([Q0]), "operationType" : NewBodyOperationType.REMOVE, "oppositeDirection" : true, "depth" : (getVariable(context, 'plugdep2')) * mm, "offsetDistance" : 25 * mm});
        }
        {
            var Q0;
            Q0=makeQuery(id+"F8.opExtrude","SWEPT_FACE",FACE,{"disambiguationData":[OSD([sQuery(id+"F7.wireOp",EDGE,"E29")])]});
            var sketch = newSketch(context, id + "F29", { "sketchPlane" : qUnion([Q0])});
            skLineSegment(sketch, "E128", {"start": v(-29.61, 31.55) * mm, "end": v(-12.72, 31.55) * mm, "construction": true});
            skLineSegment(sketch, "E129", {"start": v(-12.72, 31.55) * mm, "end": v(13.28, 31.55) * mm, "construction": true});
            skLineSegment(sketch, "E130", {"start": v(13.28, 31.55) * mm, "end": v(39.28, 31.55) * mm, "construction": true});
            skLineSegment(sketch, "E131", {"start": v(39.28, 31.55) * mm, "end": v(56.17, 31.55) * mm, "construction": true});
            skLineSegment(sketch, "E132", {"start": v(13.28, 37.1) * mm, "end": v(13.28, 26) * mm, "construction": true});
            skPoint(sketch, "E132.startSnap0", {"position": v(13.28, 36.11) * mm});
            skCircle(sketch, "E133", {"center": v(-12.72, 31.56) * mm, "radius": 3.5 * mm});
            skCircle(sketch, "E134", {"center": v(13.28, 31.56) * mm, "radius": 3.5 * mm});
            skCircle(sketch, "E135", {"center": v(39.28, 31.56) * mm, "radius": 3.5 * mm});
            skSolve(sketch);
        }
        {
            var Q0;
            Q0 = qSketchRegion(id + "F29", true);
            extrude(context, id + "F30", {"entities" : qUnion([Q0]), "operationType" : NewBodyOperationType.REMOVE, "oppositeDirection" : true, "depth" : getVariable(context, 'plugdep1'), "offsetDistance" : 25 * mm});
        }
        {
            var Q0;
            Q0=makeQuery(id+"F29.imprint","IMPRINT",FACE,{"disambiguationData":[TD([[makeQuery(id+"F29.imprint","IMPRINT",EDGE,{"derivedFrom":sQuery(id+"F29.wireOp",EDGE,"E133")}),-1.0]])]});
            var sketch = newSketch(context, id + "F31", { "sketchPlane" : qUnion([Q0])});
            skCircle(sketch, "E136", {"center": v(-12.72, 31.56) * mm, "radius": 4.2 * mm});
            skCircle(sketch, "E137", {"center": v(13.28, 31.56) * mm, "radius": 4.2 * mm});
            skCircle(sketch, "E138", {"center": v(39.28, 31.56) * mm, "radius": 4.2 * mm});
            skSolve(sketch);
        }
        {
            var Q0;
            Q0 = qSketchRegion(id + "F31", true);
            extrude(context, id + "F32", {"entities" : qUnion([Q0]), "operationType" : NewBodyOperationType.REMOVE, "oppositeDirection" : true, "depth" : (getVariable(context, 'plugdep2')) * mm, "offsetDistance" : 25 * mm});
        }
        {
            var Q0;
            Q0=makeQuery(id+"F8.opExtrude","SWEPT_FACE",FACE,{"disambiguationData":[OSD([sQuery(id+"F7.wireOp",EDGE,"E26")])]});
            var sketch = newSketch(context, id + "F33", { "sketchPlane" : qUnion([Q0])});
            skLineSegment(sketch, "E139", {"start": v(77.56, 31.56) * mm, "end": v(-52.56, 31.55) * mm, "construction": true});
            skCircle(sketch, "E140", {"center": v(-22.5, 31.55) * mm, "radius": 3.5 * mm});
            skCircle(sketch, "E141", {"center": v(12.5, 31.55) * mm, "radius": 3.5 * mm, "construction": true});
            skCircle(sketch, "E142", {"center": v(47.5, 31.55) * mm, "radius": 3.5 * mm});
            skLineSegment(sketch, "E143", {"start": v(12.5, 26) * mm, "end": v(12.5, 37.11) * mm, "construction": true});
            skSolve(sketch);
        }
        {
            var Q0;
            Q0 = qSketchRegion(id + "F33", true);
            extrude(context, id + "F34", {"entities" : qUnion([Q0]), "operationType" : NewBodyOperationType.REMOVE, "oppositeDirection" : true, "depth" : getVariable(context, 'plugdep1'), "offsetDistance" : 25 * mm});
        }
        {
            var Q0;
            Q0=makeQuery(id+"F33.imprint","IMPRINT",FACE,{"disambiguationData":[TD([[makeQuery(id+"F33.imprint","IMPRINT",EDGE,{"derivedFrom":sQuery(id+"F33.wireOp",EDGE,"E140")}),-1.0]])]});
            var sketch = newSketch(context, id + "F35", { "sketchPlane" : qUnion([Q0])});
            skCircle(sketch, "E144", {"center": v(-22.5, 31.55) * mm, "radius": 5.18 * mm});
            skCircle(sketch, "E145", {"center": v(12.5, 31.55) * mm, "radius": 5.18 * mm, "construction": true});
            skCircle(sketch, "E146", {"center": v(47.5, 31.55) * mm, "radius": 5.18 * mm});
            skSolve(sketch);
        }
        {
            var Q0;
            Q0 = qSketchRegion(id + "F35", true);
            extrude(context, id + "F36", {"entities" : qUnion([Q0]), "operationType" : NewBodyOperationType.REMOVE, "oppositeDirection" : true, "depth" : (getVariable(context, 'plugdep2')) * mm, "offsetDistance" : 25 * mm});
        }
        {
            var Q0;
            Q0=makeQuery(id+"F8.opExtrude","CAP_FACE",FACE,{"disambiguationData":[OSD([sQuery(id+"F7.wireOp",EDGE,"E24"),sQuery(id+"F7.wireOp",EDGE,"E25"),sQuery(id+"F7.wireOp",EDGE,"E26"),sQuery(id+"F7.wireOp",EDGE,"E27"),sQuery(id+"F7.wireOp",EDGE,"E28"),sQuery(id+"F7.wireOp",EDGE,"E29"),sQuery(id+"F7.wireOp",EDGE,"E30"),sQuery(id+"F7.wireOp",EDGE,"E31"),sQuery(id+"F7.wireOp",EDGE,"E32"),sQuery(id+"F7.wireOp",EDGE,"E33"),sQuery(id+"F7.wireOp",EDGE,"E44"),sQuery(id+"F7.wireOp",EDGE,"E45"),sQuery(id+"F7.wireOp",EDGE,"E46"),sQuery(id+"F7.wireOp",EDGE,"E47"),sQuery(id+"F7.wireOp",EDGE,"E48"),sQuery(id+"F7.wireOp",EDGE,"E49"),sQuery(id+"F7.wireOp",EDGE,"E62"),sQuery(id+"F7.wireOp",EDGE,"E63"),sQuery(id+"F7.wireOp",EDGE,"E64"),sQuery(id+"F7.wireOp",EDGE,"E65")])],"isStart":false});
            var sketch = newSketch(context, id + "F37", { "sketchPlane" : qUnion([Q0])});
            skLineSegment(sketch, "E147", {"start": v(-16.25, 54.33) * mm, "end": v(-12.25, 50.33) * mm});
            skLineSegment(sketch, "E148", {"start": v(-12.25, 50.33) * mm, "end": v(-12.25, 45.33) * mm});
            skLineSegment(sketch, "E149", {"start": v(-12.25, 45.33) * mm, "end": v(-16.25, 41.33) * mm});
            skLineSegment(sketch, "E150", {"start": v(-16.75, 41.33) * mm, "end": v(-16.25, 41.33) * mm});
            skLineSegment(sketch, "E151", {"start": v(-16.75, 41.33) * mm, "end": v(-12.75, 45.33) * mm});
            skLineSegment(sketch, "E152", {"start": v(-12.75, 45.33) * mm, "end": v(-12.75, 50.33) * mm});
            skLineSegment(sketch, "E153", {"start": v(-12.75, 50.33) * mm, "end": v(-16.75, 54.33) * mm});
            skLineSegment(sketch, "E154", {"start": v(-16.25, 54.33) * mm, "end": v(-16.75, 54.33) * mm});
            skLineSegment(sketch, "E155", {"start": v(-12.75, 47.83) * mm, "end": v(-12.25, 47.83) * mm, "construction": true});
            skPoint(sketch, "E156", {"position": v(-12.5, 47.83) * mm});
            skPoint(sketch, "E157", {"position": v(-12.5, 50.33) * mm});
            skLineSegment(sketch, "E158", {"start": v(-16.75, -67.32) * mm, "end": v(-12.75, -71.32) * mm});
            skLineSegment(sketch, "E159", {"start": v(-12.75, -71.32) * mm, "end": v(-12.75, -80.32) * mm});
            skLineSegment(sketch, "E160", {"start": v(-12.75, -80.32) * mm, "end": v(-16.75, -84.32) * mm});
            skLineSegment(sketch, "E161", {"start": v(-16.75, -84.32) * mm, "end": v(-16.25, -84.32) * mm});
            skLineSegment(sketch, "E162", {"start": v(-16.25, -84.32) * mm, "end": v(-12.25, -80.32) * mm});
            skLineSegment(sketch, "E163", {"start": v(-12.25, -80.32) * mm, "end": v(-12.25, -71.32) * mm});
            skLineSegment(sketch, "E164", {"start": v(-12.25, -71.32) * mm, "end": v(-16.25, -67.32) * mm});
            skLineSegment(sketch, "E165", {"start": v(-16.25, -67.32) * mm, "end": v(-16.75, -67.32) * mm});
            skLineSegment(sketch, "E166", {"start": v(-12.75, -75.82) * mm, "end": v(-12.25, -75.82) * mm, "construction": true});
            skPoint(sketch, "E167", {"position": v(-12.5, -75.82) * mm});
            skPoint(sketch, "E168", {"position": v(-12.5, -80.32) * mm});
            skSolve(sketch);
        }
        {
            var Q0;
            Q0 = qSketchRegion(id + "F37", true);
            var Q1;
            Q1=makeQuery(id+"F8.opExtrude","CAP_FACE",FACE,{"disambiguationData":[OSD([sQuery(id+"F7.wireOp",EDGE,"E24"),sQuery(id+"F7.wireOp",EDGE,"E25"),sQuery(id+"F7.wireOp",EDGE,"E26"),sQuery(id+"F7.wireOp",EDGE,"E27"),sQuery(id+"F7.wireOp",EDGE,"E28"),sQuery(id+"F7.wireOp",EDGE,"E29"),sQuery(id+"F7.wireOp",EDGE,"E30"),sQuery(id+"F7.wireOp",EDGE,"E31"),sQuery(id+"F7.wireOp",EDGE,"E32"),sQuery(id+"F7.wireOp",EDGE,"E33"),sQuery(id+"F7.wireOp",EDGE,"E44"),sQuery(id+"F7.wireOp",EDGE,"E45"),sQuery(id+"F7.wireOp",EDGE,"E46"),sQuery(id+"F7.wireOp",EDGE,"E47"),sQuery(id+"F7.wireOp",EDGE,"E48"),sQuery(id+"F7.wireOp",EDGE,"E49"),sQuery(id+"F7.wireOp",EDGE,"E62"),sQuery(id+"F7.wireOp",EDGE,"E63"),sQuery(id+"F7.wireOp",EDGE,"E64"),sQuery(id+"F7.wireOp",EDGE,"E65")])],"isStart":true});
            extrude(context, id + "F38", {"entities" : qUnion([Q0]), "operationType" : NewBodyOperationType.REMOVE, "endBound" : BoundingType.UP_TO_SURFACE, "oppositeDirection" : true, "depth" : 25 * mm, "endBoundEntityFace" : qUnion([Q1]), "offsetDistance" : 25 * mm});
        }
    });
